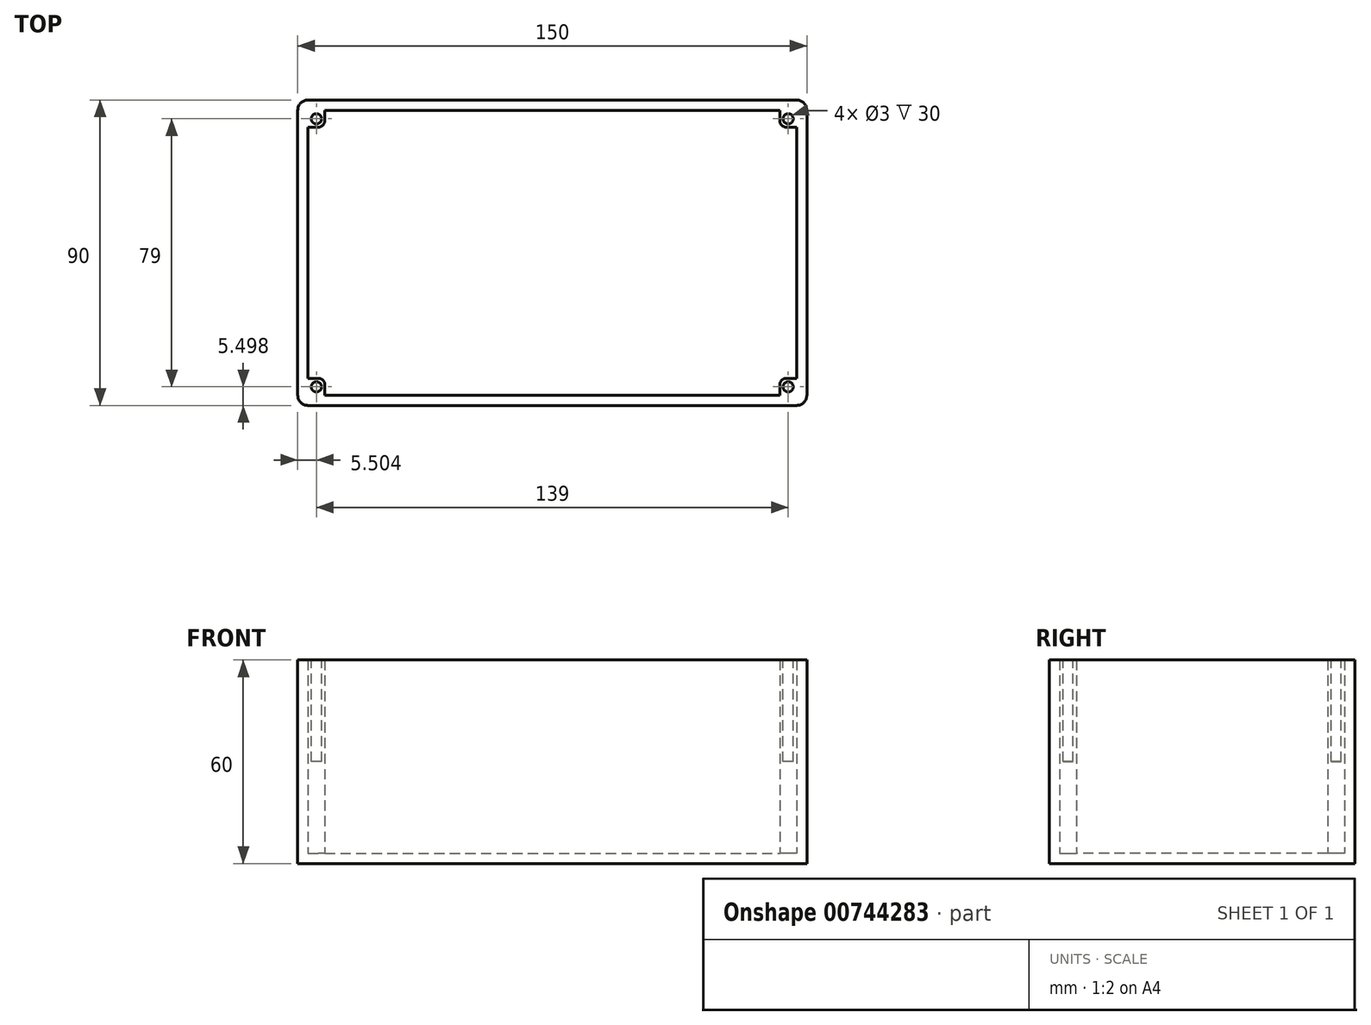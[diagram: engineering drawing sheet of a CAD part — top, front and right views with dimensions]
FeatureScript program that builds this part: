
annotation { "Feature Type Name" : "Feature", "Feature Type Description" : "" }
export const myFeature = defineFeature(function(context is Context, id is Id, definition is map)
    precondition{}
    {
        {
            var Q0;
            Q0=qCreatedBy(makeId("Top.planeOp"),FACE);
            var sketch = newSketch(context, id + "F0", { "sketchPlane" : qUnion([Q0])});
            skLineSegment(sketch, "E0.bottom", {"start": v(-70.55, 42.44) * mm, "end": v(79.45, 42.44) * mm});
            skLineSegment(sketch, "E0.top", {"start": v(-70.55, -47.56) * mm, "end": v(79.45, -47.56) * mm});
            skLineSegment(sketch, "E0.left", {"start": v(-70.55, 42.44) * mm, "end": v(-70.55, -47.56) * mm});
            skLineSegment(sketch, "E0.right", {"start": v(79.45, 42.44) * mm, "end": v(79.45, -47.56) * mm});
            skLineSegment(sketch, "E1.bottom", {"start": v(-67.55, 39.44) * mm, "end": v(76.45, 39.44) * mm});
            skLineSegment(sketch, "E1.top", {"start": v(-67.55, -44.56) * mm, "end": v(76.45, -44.56) * mm});
            skLineSegment(sketch, "E1.left", {"start": v(-67.55, 39.44) * mm, "end": v(-67.55, -44.56) * mm});
            skLineSegment(sketch, "E1.right", {"start": v(76.45, 39.44) * mm, "end": v(76.45, -44.56) * mm});
            skSolve(sketch);
        }
        {
            var Q0;
            Q0=makeQuery(id+"F0.imprint","IMPRINT",FACE,{"disambiguationData":[TD([[makeQuery(id+"F0.imprint","IMPRINT",EDGE,{"derivedFrom":sQuery(id+"F0.wireOp",EDGE,"E1.bottom")}),-1.0]])]});
            extrude(context, id + "F1", {"entities" : qUnion([Q0]), "depth" : 3 * mm, "offsetDistance" : 25 * mm});
        }
        {
            var Q0;
            Q0 = qSketchRegion(id + "F0", true);
            extrude(context, id + "F2", {"entities" : qUnion([Q0]), "operationType" : NewBodyOperationType.ADD, "depth" : 60 * mm, "offsetDistance" : 25 * mm});
        }
        {
            var Q0;
            Q0=makeQuery(id+"F2.opExtrude","SWEPT_EDGE",EDGE,{"disambiguationData":[OSD([sQuery(id+"F0.wireOp",EDGE,"E0.bottom"),sQuery(id+"F0.wireOp",EDGE,"E0.left")])]});
            var Q1;
            Q1=makeQuery(id+"F2.opExtrude","SWEPT_EDGE",EDGE,{"disambiguationData":[OSD([sQuery(id+"F0.wireOp",EDGE,"E0.top"),sQuery(id+"F0.wireOp",EDGE,"E0.left")])]});
            var Q2;
            Q2=makeQuery(id+"F2.opExtrude","SWEPT_EDGE",EDGE,{"disambiguationData":[OSD([sQuery(id+"F0.wireOp",EDGE,"E0.top"),sQuery(id+"F0.wireOp",EDGE,"E0.right")])]});
            var Q3;
            Q3=makeQuery(id+"F2.opExtrude","SWEPT_EDGE",EDGE,{"disambiguationData":[OSD([sQuery(id+"F0.wireOp",EDGE,"E0.bottom"),sQuery(id+"F0.wireOp",EDGE,"E0.right")])]});
            fillet(context, id + "F3", {"entities" : qUnion([Q0, Q1, Q2, Q3]), "radius" : 3 * mm, "tangentPropagation" : true, "allowEdgeOverflow" : false});
        }
        {
            var Q0;
            Q0=makeQuery(id+"F1.opExtrude","CAP_FACE",FACE,{"disambiguationData":[OSD([sQuery(id+"F0.wireOp",EDGE,"E1.bottom"),sQuery(id+"F0.wireOp",EDGE,"E1.top"),sQuery(id+"F0.wireOp",EDGE,"E1.left"),sQuery(id+"F0.wireOp",EDGE,"E1.right")])],"isStart":false});
            var sketch = newSketch(context, id + "F4", { "sketchPlane" : qUnion([Q0])});
            skLineSegment(sketch, "E2.bottom", {"start": v(-67.55, 39.44) * mm, "end": v(-62.55, 39.44) * mm});
            skLineSegment(sketch, "E2.top", {"start": v(-67.55, 34.44) * mm, "end": v(-62.55, 34.44) * mm});
            skLineSegment(sketch, "E2.left", {"start": v(-67.55, 39.44) * mm, "end": v(-67.55, 34.44) * mm});
            skLineSegment(sketch, "E2.right", {"start": v(-62.55, 39.44) * mm, "end": v(-62.55, 34.44) * mm});
            skLineSegment(sketch, "E3.bottom", {"start": v(76.45, 39.44) * mm, "end": v(71.45, 39.44) * mm});
            skLineSegment(sketch, "E3.top", {"start": v(76.45, 34.44) * mm, "end": v(71.45, 34.44) * mm});
            skLineSegment(sketch, "E3.left", {"start": v(76.45, 39.44) * mm, "end": v(76.45, 34.44) * mm});
            skLineSegment(sketch, "E3.right", {"start": v(71.45, 39.44) * mm, "end": v(71.45, 34.44) * mm});
            skLineSegment(sketch, "E4.bottom", {"start": v(76.45, -44.56) * mm, "end": v(71.45, -44.56) * mm});
            skLineSegment(sketch, "E4.top", {"start": v(76.45, -39.56) * mm, "end": v(71.45, -39.56) * mm});
            skLineSegment(sketch, "E4.left", {"start": v(76.45, -44.56) * mm, "end": v(76.45, -39.56) * mm});
            skLineSegment(sketch, "E4.right", {"start": v(71.45, -44.56) * mm, "end": v(71.45, -39.56) * mm});
            skLineSegment(sketch, "E5.bottom", {"start": v(-67.55, -44.56) * mm, "end": v(-62.55, -44.56) * mm});
            skLineSegment(sketch, "E5.top", {"start": v(-67.55, -39.56) * mm, "end": v(-62.55, -39.56) * mm});
            skLineSegment(sketch, "E5.left", {"start": v(-67.55, -44.56) * mm, "end": v(-67.55, -39.56) * mm});
            skLineSegment(sketch, "E5.right", {"start": v(-62.55, -44.56) * mm, "end": v(-62.55, -39.56) * mm});
            skSolve(sketch);
        }
        {
            var Q0;
            Q0=makeQuery(id+"F4.imprint","IMPRINT",FACE,{"disambiguationData":[TD([[makeQuery(id+"F4.imprint","IMPRINT",EDGE,{"derivedFrom":sQuery(id+"F4.wireOp",EDGE,"E2.bottom")}),-1.0]])]});
            var Q1;
            Q1=makeQuery(id+"F4.imprint","IMPRINT",FACE,{"disambiguationData":[TD([[makeQuery(id+"F4.imprint","IMPRINT",EDGE,{"derivedFrom":sQuery(id+"F4.wireOp",EDGE,"E5.bottom")}),1.0]])]});
            var Q2;
            Q2=makeQuery(id+"F4.imprint","IMPRINT",FACE,{"disambiguationData":[TD([[makeQuery(id+"F4.imprint","IMPRINT",EDGE,{"derivedFrom":sQuery(id+"F4.wireOp",EDGE,"E3.bottom")}),-1.0]])]});
            var Q3;
            Q3=makeQuery(id+"F4.imprint","IMPRINT",FACE,{"disambiguationData":[TD([[makeQuery(id+"F4.imprint","IMPRINT",EDGE,{"derivedFrom":sQuery(id+"F4.wireOp",EDGE,"E4.bottom")}),1.0]])]});
            extrude(context, id + "F5", {"entities" : qUnion([Q0, Q1, Q2, Q3]), "operationType" : NewBodyOperationType.ADD, "depth" : 57 * mm, "offsetDistance" : 25 * mm});
        }
        {
            var Q0;
            Q0=makeQuery(id+"F5.boolean.opBoolean","MERGE",FACE,{"derivedFrom":[makeQuery(id+"F2.opExtrude","CAP_FACE",FACE,{"disambiguationData":[OSD([sQuery(id+"F0.wireOp",EDGE,"E0.bottom"),sQuery(id+"F0.wireOp",EDGE,"E0.top"),sQuery(id+"F0.wireOp",EDGE,"E0.left"),sQuery(id+"F0.wireOp",EDGE,"E0.right"),sQuery(id+"F0.wireOp",EDGE,"E1.bottom"),sQuery(id+"F0.wireOp",EDGE,"E1.top"),sQuery(id+"F0.wireOp",EDGE,"E1.left"),sQuery(id+"F0.wireOp",EDGE,"E1.right")])],"isStart":false}),makeQuery(id+"F5.opExtrude","CAP_FACE",FACE,{"disambiguationData":[OSD([sQuery(id+"F4.wireOp",EDGE,"E2.bottom"),sQuery(id+"F4.wireOp",EDGE,"E2.top"),sQuery(id+"F4.wireOp",EDGE,"E2.left"),sQuery(id+"F4.wireOp",EDGE,"E2.right")])],"isStart":false}),makeQuery(id+"F5.opExtrude","CAP_FACE",FACE,{"disambiguationData":[OSD([sQuery(id+"F4.wireOp",EDGE,"E3.bottom"),sQuery(id+"F4.wireOp",EDGE,"E3.top"),sQuery(id+"F4.wireOp",EDGE,"E3.left"),sQuery(id+"F4.wireOp",EDGE,"E3.right")])],"isStart":false}),makeQuery(id+"F5.opExtrude","CAP_FACE",FACE,{"disambiguationData":[OSD([sQuery(id+"F4.wireOp",EDGE,"E4.bottom"),sQuery(id+"F4.wireOp",EDGE,"E4.top"),sQuery(id+"F4.wireOp",EDGE,"E4.left"),sQuery(id+"F4.wireOp",EDGE,"E4.right")])],"isStart":false}),makeQuery(id+"F5.opExtrude","CAP_FACE",FACE,{"disambiguationData":[OSD([sQuery(id+"F4.wireOp",EDGE,"E5.bottom"),sQuery(id+"F4.wireOp",EDGE,"E5.top"),sQuery(id+"F4.wireOp",EDGE,"E5.left"),sQuery(id+"F4.wireOp",EDGE,"E5.right")])],"isStart":false})]});
            var sketch = newSketch(context, id + "F6", { "sketchPlane" : qUnion([Q0])});
            skCircle(sketch, "E6", {"center": v(-65.05, 36.94) * mm, "radius": 1.5 * mm});
            skCircle(sketch, "E7", {"center": v(-65.05, -42.06) * mm, "radius": 1.5 * mm});
            skPoint(sketch, "E7.centerSnap0", {"position": v(-62.55, -42.06) * mm});
            skPoint(sketch, "E7.centerSnap1", {"position": v(-65.05, -39.56) * mm});
            skCircle(sketch, "E8", {"center": v(73.95, -42.06) * mm, "radius": 1.5 * mm});
            skPoint(sketch, "E8.centerSnap0", {"position": v(73.95, -39.56) * mm});
            skPoint(sketch, "E8.centerSnap1", {"position": v(71.45, -42.06) * mm});
            skCircle(sketch, "E9", {"center": v(73.95, 36.94) * mm, "radius": 1.5 * mm});
            skPoint(sketch, "E9.centerSnap0", {"position": v(71.45, 36.94) * mm});
            skPoint(sketch, "E9.centerSnap1", {"position": v(73.95, 34.44) * mm});
            skSolve(sketch);
        }
        {
            var Q0;
            Q0=makeQuery(id+"F6.imprint","IMPRINT",FACE,{"disambiguationData":[TD([[makeQuery(id+"F6.imprint","IMPRINT",EDGE,{"derivedFrom":sQuery(id+"F6.wireOp",EDGE,"E6")}),1.0]])]});
            var Q1;
            Q1=makeQuery(id+"F6.imprint","IMPRINT",FACE,{"disambiguationData":[TD([[makeQuery(id+"F6.imprint","IMPRINT",EDGE,{"derivedFrom":sQuery(id+"F6.wireOp",EDGE,"E7")}),1.0]])]});
            var Q2;
            Q2=makeQuery(id+"F6.imprint","IMPRINT",FACE,{"disambiguationData":[TD([[makeQuery(id+"F6.imprint","IMPRINT",EDGE,{"derivedFrom":sQuery(id+"F6.wireOp",EDGE,"E8")}),1.0]])]});
            var Q3;
            Q3=makeQuery(id+"F6.imprint","IMPRINT",FACE,{"disambiguationData":[TD([[makeQuery(id+"F6.imprint","IMPRINT",EDGE,{"derivedFrom":sQuery(id+"F6.wireOp",EDGE,"E9")}),1.0]])]});
            extrude(context, id + "F7", {"entities" : qUnion([Q0, Q1, Q2, Q3]), "operationType" : NewBodyOperationType.REMOVE, "oppositeDirection" : true, "depth" : 30 * mm, "offsetDistance" : 25 * mm});
        }
        {
            var Q0;
            Q0=makeQuery(id+"F5.opExtrude","SWEPT_EDGE",EDGE,{"disambiguationData":[OSD([sQuery(id+"F4.wireOp",EDGE,"E2.top"),sQuery(id+"F4.wireOp",EDGE,"E2.right")])]});
            var Q1;
            Q1=makeQuery(id+"F5.opExtrude","SWEPT_EDGE",EDGE,{"disambiguationData":[OSD([sQuery(id+"F4.wireOp",EDGE,"E3.top"),sQuery(id+"F4.wireOp",EDGE,"E3.right")])]});
            var Q2;
            Q2=makeQuery(id+"F5.opExtrude","SWEPT_EDGE",EDGE,{"disambiguationData":[OSD([sQuery(id+"F4.wireOp",EDGE,"E4.top"),sQuery(id+"F4.wireOp",EDGE,"E4.right")])]});
            var Q3;
            Q3=makeQuery(id+"F5.opExtrude","SWEPT_EDGE",EDGE,{"disambiguationData":[OSD([sQuery(id+"F4.wireOp",EDGE,"E5.top"),sQuery(id+"F4.wireOp",EDGE,"E5.right")])]});
            fillet(context, id + "F8", {"entities" : qUnion([Q0, Q1, Q2, Q3]), "radius" : 2 * mm, "tangentPropagation" : true, "allowEdgeOverflow" : false});
        }
    });
